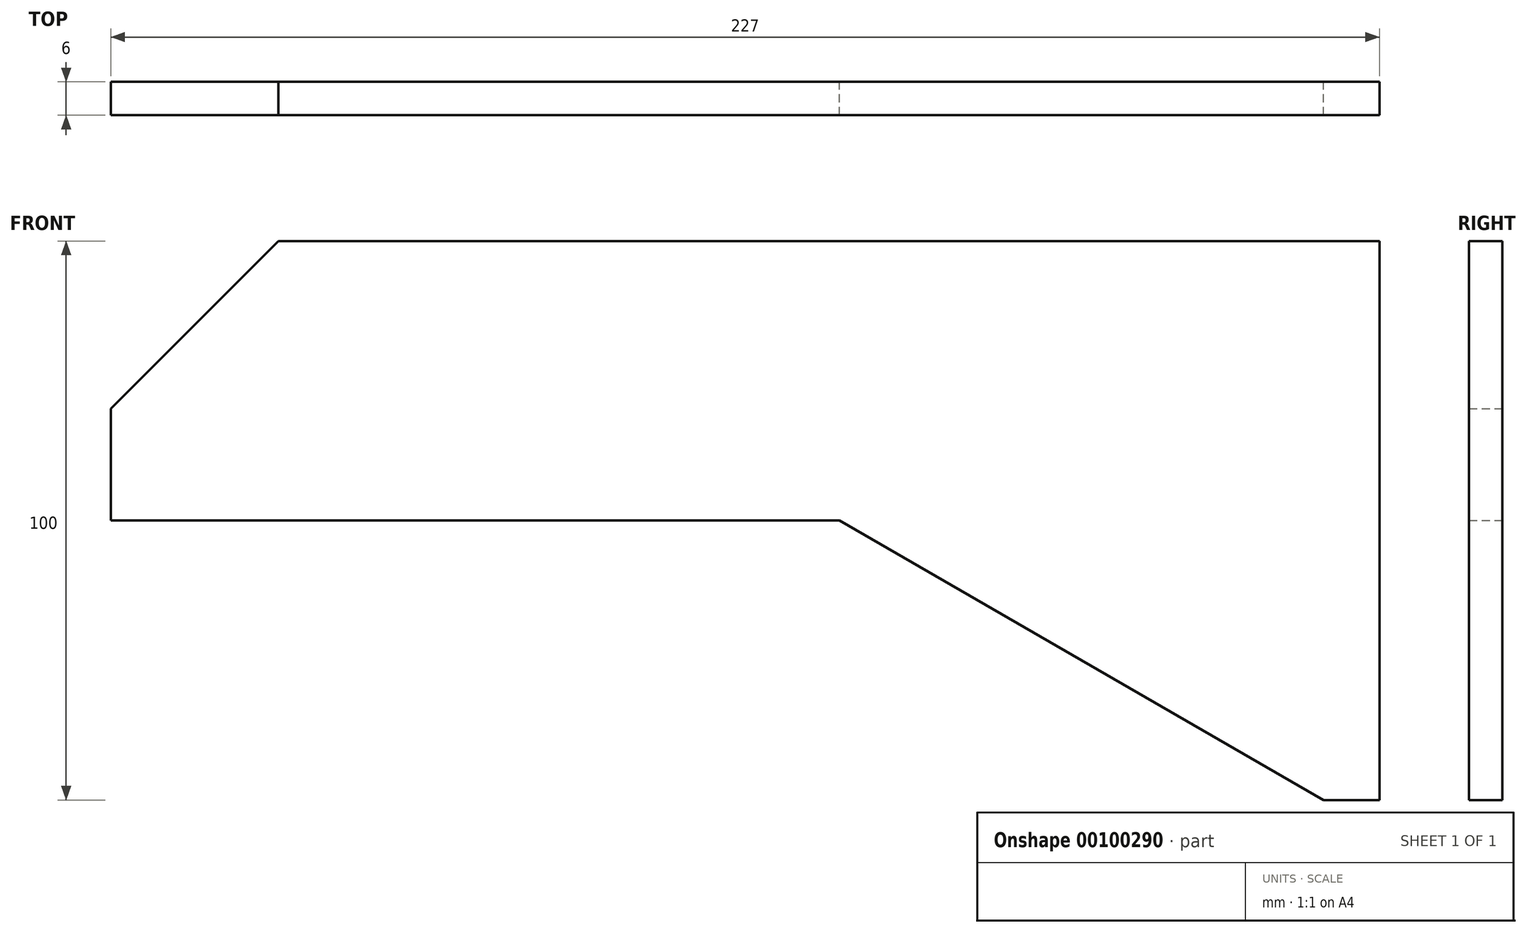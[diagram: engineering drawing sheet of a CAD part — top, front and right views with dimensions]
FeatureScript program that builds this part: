
annotation { "Feature Type Name" : "Feature", "Feature Type Description" : "" }
export const myFeature = defineFeature(function(context is Context, id is Id, definition is map)
    precondition{}
    {
        {
            var Q0;
            Q0=qCreatedBy(makeId("Front.planeOp"),FACE);
            var sketch = newSketch(context, id + "F0", { "sketchPlane" : qUnion([Q0])});
            skLineSegment(sketch, "E0.bottom", {"start": v(0, 50) * mm, "end": v(-227, 50) * mm});
            skPoint(sketch, "E1.start.orphan", {"position": v(0, 0) * mm});
            skLineSegment(sketch, "E2", {"start": v(-227, 50) * mm, "end": v(-227, 0) * mm});
            skLineSegment(sketch, "E3", {"start": v(0, 50) * mm, "end": v(0, -50) * mm});
            skLineSegment(sketch, "E4", {"start": v(0, -50) * mm, "end": v(-10, -50) * mm});
            skLineSegment(sketch, "E5", {"start": v(-10, -50) * mm, "end": v(-96.6, 0) * mm});
            skLineSegment(sketch, "E6.trimOffspring", {"start": v(-96.6, 0) * mm, "end": v(-227, 0) * mm});
            skSolve(sketch);
        }
        {
            var Q0;
            Q0=makeQuery(id+"F0.imprint","IMPRINT",FACE,{"disambiguationData":[TD([[makeQuery(id+"F0.imprint","IMPRINT",EDGE,{"derivedFrom":sQuery(id+"F0.wireOp",EDGE,"E0.bottom")}),1.0]])]});
            extrude(context, id + "F1", {"entities" : qUnion([Q0]), "endBound" : BoundingType.SYMMETRIC, "depth" : 6 * mm});
        }
        {
            var Q0;
            Q0=makeQuery(id+"F1.opExtrude","SWEPT_EDGE",EDGE,{"disambiguationData":[OSD([sQuery(id+"F0.wireOp",EDGE,"E0.bottom"),sQuery(id+"F0.wireOp",EDGE,"E2")])]});
            chamfer(context, id + "F2", {"entities" : qUnion([Q0]), "width" : 30 * mm, "tangentPropagation" : true});
        }
    });
